# Revit family: Faucet-Kitchen-KOHLER-Karbon-K-6227K_1
name_source: partatom
category: Plumbing Fixtures
revit_build: Autodesk Revit 2017 (Build: 20160225_1515(x64)
units: mm (PartAtom-declared; Revit-internal decimal feet)

## family parameters
Cut with Voids When Loaded = No
Host = Face
OmniClass Number = 23.31.11.00
OmniClass Title = Faucets
Part Type = Normal
Room Calculation Point = No
Round Connector Dimension = Use Diameter
Shared = No

## types (2) — shared parameters
ADA Compliant = No
Assembly Code = D2010
CW Connection = Yes
Cold Water Inlet = Cold Water Inlet
Date Modified = 07/20/2020
Default Elevation = 36"
Description = Deck-Mount Kitchen Faucet
Drain Included = No
Flow Rate = 2 GPM
HW Connection = Yes
Height = 8 15/16"
Hot Water Inlet = Hot Water Inlet
Length = 13 1/4"
Manufacturer = KOHLER Co.
MasterFormat 2014 = 22.41.39
MasterFormat 2014 Name = Residential Faucets, Supplies, and Trim
Material = Premium Metal and Carbon Fiber Construction
Pressure = 60.00 psi
Product Documentation Link = http://resources.kohler.com
Product Name = Karbon
Product Page URL = https://www.kohlerasiapacific.com
Spout Reach = 13 1/4"
Tube_Material = Kohler-Fiber-C11-Silver
URL = https://www.kohlerasiapacific.com
Vent Connection = No
Waste Connection = No
Waste Water Outlet = Waste Water Outlet
WaterSense Certified = No
Width = 2 5/8"

## per-type parameters (varying)
| type | Finish | Model | Type |
| CP-Polished Chrome | Kohler-Metal-CP-Polished_Chrome | K-6227K-CP | 1 |
| VS-Vibrant Stainless | Kohler-Metal-VS-Vibrant_Stainless | K-6227K-VS | 2 |

## geometry (parser evidence)
native form markers: Sweep x6
no freeform markers — native parametric forms only
